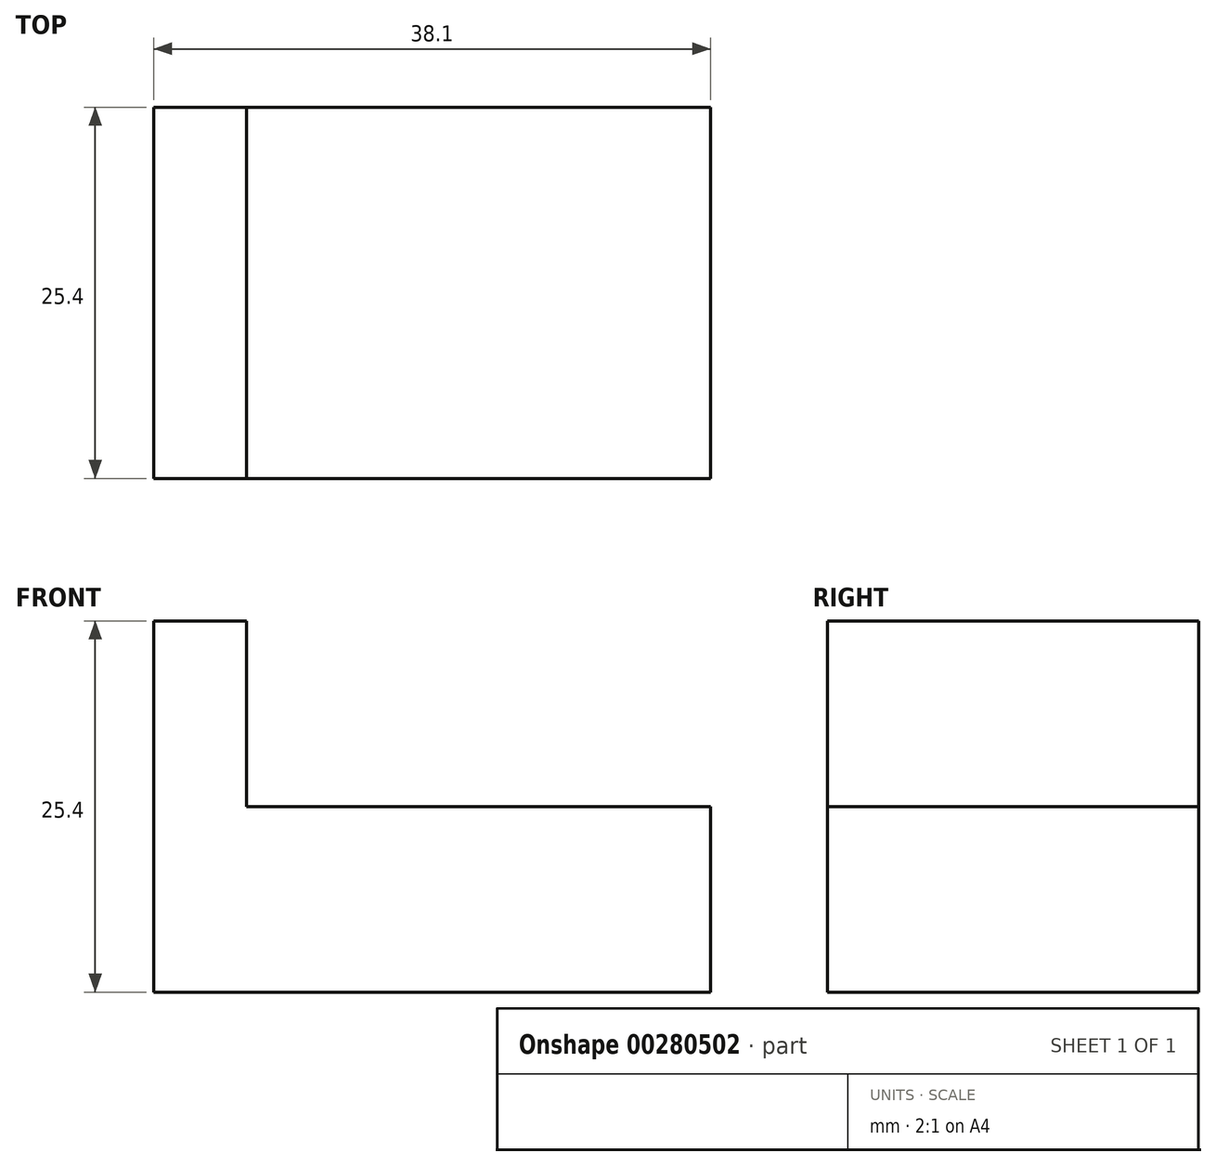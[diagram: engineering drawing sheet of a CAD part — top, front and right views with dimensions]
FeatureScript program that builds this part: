
annotation { "Feature Type Name" : "Feature", "Feature Type Description" : "" }
export const myFeature = defineFeature(function(context is Context, id is Id, definition is map)
    precondition{}
    {
        {
            var Q0;
            Q0=qCreatedBy(makeId("Front.planeOp"),FACE);
            var sketch = newSketch(context, id + "F0", { "sketchPlane" : qUnion([Q0])});
            skLineSegment(sketch, "E0", {"start": v(0, 25.4) * mm, "end": v(0, 0) * mm});
            skLineSegment(sketch, "E1", {"start": v(0, 0) * mm, "end": v(0, 25.4) * mm});
            skLineSegment(sketch, "E2", {"start": v(6.35, 25.4) * mm, "end": v(6.35, 12.7) * mm});
            skLineSegment(sketch, "E3", {"start": v(6.35, 12.7) * mm, "end": v(38.1, 12.7) * mm});
            skLineSegment(sketch, "E4", {"start": v(38.1, 12.7) * mm, "end": v(38.1, 0) * mm});
            skLineSegment(sketch, "E5", {"start": v(38.1, 0) * mm, "end": v(0, 0) * mm});
            skLineSegment(sketch, "E6", {"start": v(0, 25.4) * mm, "end": v(6.35, 25.4) * mm});
            skSolve(sketch);
        }
        {
            var Q0;
            Q0 = qSketchRegion(id + "F0", true);
            extrude(context, id + "F1", {"entities" : qUnion([Q0]), "depth" : 25.4 * mm});
        }
    });
